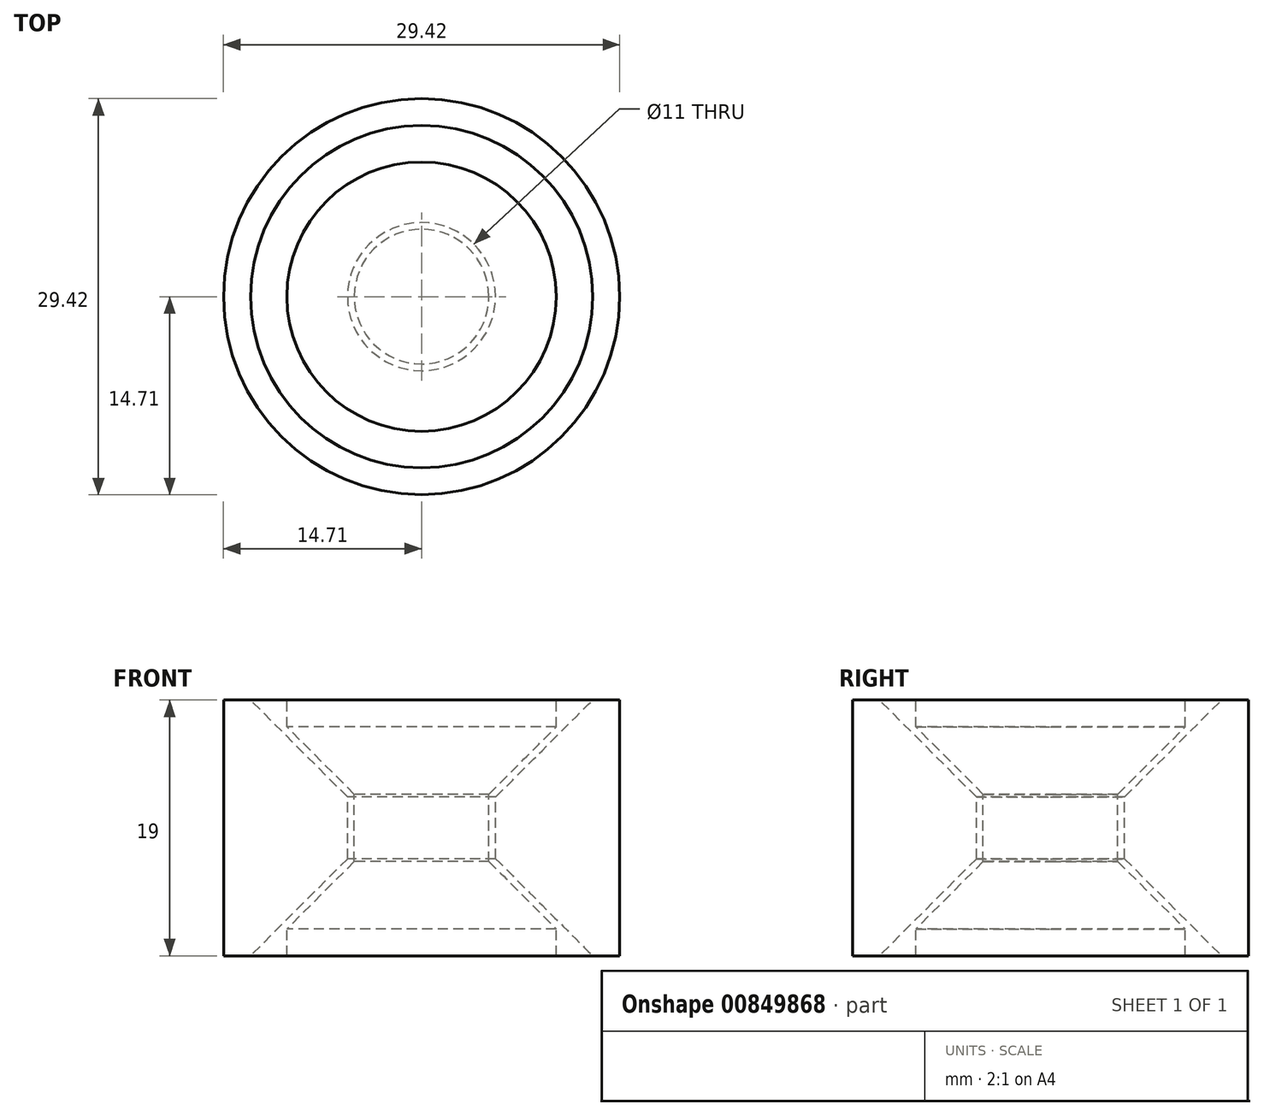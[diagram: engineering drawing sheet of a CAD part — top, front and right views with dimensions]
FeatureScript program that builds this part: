
annotation { "Feature Type Name" : "Feature", "Feature Type Description" : "" }
export const myFeature = defineFeature(function(context is Context, id is Id, definition is map)
    precondition{}
    {
        {
            var Q0;
            Q0=qCreatedBy(makeId("Front.planeOp"),FACE);
            var sketch = newSketch(context, id + "F0", { "sketchPlane" : qUnion([Q0])});
            skLineSegment(sketch, "E0", {"start": v(0, 0) * mm, "end": v(10, 0) * mm});
            skLineSegment(sketch, "E1", {"start": v(10, 0) * mm, "end": v(10, 2) * mm});
            skLineSegment(sketch, "E2", {"start": v(10, 2) * mm, "end": v(5, 7) * mm});
            skLineSegment(sketch, "E3", {"start": v(10, 2) * mm, "end": v(0, 2) * mm, "construction": true});
            skLineSegment(sketch, "E4", {"start": v(5, 7) * mm, "end": v(5, 2) * mm, "construction": true});
            skLineSegment(sketch, "E5", {"start": v(5, 7) * mm, "end": v(5, 12) * mm});
            skLineSegment(sketch, "E6", {"start": v(0, 9.5) * mm, "end": v(5, 9.5) * mm, "construction": true});
            skLineSegment(sketch, "E7.MirrorCS", {"start": v(0, 19) * mm, "end": v(10, 19) * mm});
            skLineSegment(sketch, "E8.MirrorCS", {"start": v(10, 17) * mm, "end": v(5, 12) * mm});
            skLineSegment(sketch, "E9.MirrorCS", {"start": v(10, 19) * mm, "end": v(10, 17) * mm});
            skLineSegment(sketch, "E10", {"start": v(0, 19) * mm, "end": v(0, 0) * mm});
            skLineSegment(sketch, "E11.0", {"start": v(12.7, 0) * mm, "end": v(5.5, 7.2) * mm});
            skLineSegment(sketch, "E11.1", {"start": v(5.5, 7.2) * mm, "end": v(5.5, 11.8) * mm});
            skLineSegment(sketch, "E11.2", {"start": v(12.7, 19) * mm, "end": v(5.5, 11.8) * mm});
            skLineSegment(sketch, "E12", {"start": v(10, 19) * mm, "end": v(17.94, 19) * mm, "construction": true});
            skLineSegment(sketch, "E13", {"start": v(10, 0) * mm, "end": v(17.94, 0) * mm, "construction": true});
            skLineSegment(sketch, "E14", {"start": v(12.7, 19) * mm, "end": v(14.7, 19) * mm});
            skLineSegment(sketch, "E15", {"start": v(12.7, 0) * mm, "end": v(14.7, 0) * mm});
            skLineSegment(sketch, "E16", {"start": v(14.7, 0) * mm, "end": v(14.7, 19) * mm});
            skSolve(sketch);
        }
        {
            var Q0;
            Q0=makeQuery(id+"F0.imprint","IMPRINT",FACE,{"disambiguationData":[TD([[makeQuery(id+"F0.imprint","IMPRINT",EDGE,{"derivedFrom":sQuery(id+"F0.wireOp",EDGE,"E0")}),1.0]])]});
            var Q1;
            Q1=makeQuery(id+"F0.imprint","IMPRINT",FACE,{"disambiguationData":[TD([[makeQuery(id+"F0.imprint","IMPRINT",EDGE,{"derivedFrom":sQuery(id+"F0.wireOp",EDGE,"E11.0")}),-1.0]])]});
            var Q2;
            Q2=sQuery(id+"F0.wireOp",EDGE,"E10");
            revolve(context, id + "F1", {"surfaceOperationType" : NewSurfaceOperationType.NEW, "entities" : qUnion([Q0, Q1]), "axis" : qUnion([Q2]), "revolveType" : RevolveType.FULL});
        }
    });
